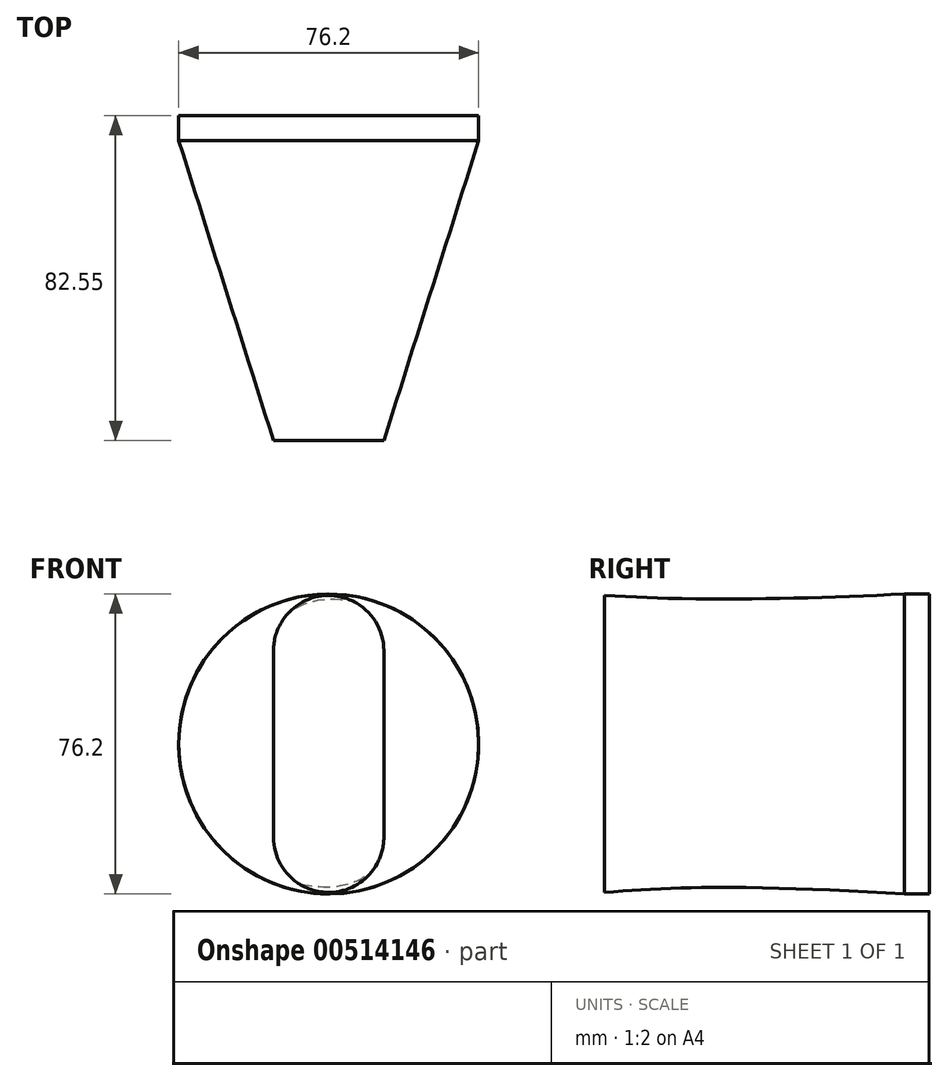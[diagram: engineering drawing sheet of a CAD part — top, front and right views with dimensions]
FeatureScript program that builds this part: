
annotation { "Feature Type Name" : "Feature", "Feature Type Description" : "" }
export const myFeature = defineFeature(function(context is Context, id is Id, definition is map)
    precondition{}
    {
        {
            var Q0;
            Q0=qCreatedBy(makeId("Front.planeOp"),FACE);
            var sketch = newSketch(context, id + "F0", { "sketchPlane" : qUnion([Q0])});
            skCircle(sketch, "E0", {"center": v(0, 0) * mm, "radius": 38.1 * mm});
            skSolve(sketch);
        }
        {
            var Q0;
            Q0=makeQuery(id+"F0.imprint","IMPRINT",FACE,{"disambiguationData":[TD([[makeQuery(id+"F0.imprint","IMPRINT",EDGE,{"derivedFrom":sQuery(id+"F0.wireOp",EDGE,"E0")}),1.0]])]});
            extrude(context, id + "F1", {"entities" : qUnion([Q0]), "oppositeDirection" : true, "depth" : 6.35 * mm, "offsetDistance" : 25.4 * mm});
        }
        {
            var Q0;
            Q0=qCreatedBy(makeId("Front.planeOp"),FACE);
            cPlane(context, id + "F2", {"entities" : qUnion([Q0]), "cplaneType" : CPlaneType.OFFSET, "offset" : 76.2 * mm, "width" : 152.4 * mm, "height" : 152.4 * mm});
        }
        {
            var Q0;
            Q0=qCreatedBy(id+"F2.planeOp",FACE);
            var sketch = newSketch(context, id + "F3", { "sketchPlane" : qUnion([Q0])});
            skLineSegment(sketch, "E1.bottom", {"start": v(-14.01, 23.7) * mm, "end": v(14.01, 23.7) * mm, "construction": true});
            skLineSegment(sketch, "E1.top", {"start": v(-14.01, -23.7) * mm, "end": v(14.01, -23.7) * mm, "construction": true});
            skLineSegment(sketch, "E1.left", {"start": v(-14.01, 23.7) * mm, "end": v(-14.01, -23.7) * mm});
            skLineSegment(sketch, "E1.right", {"start": v(14.01, 23.7) * mm, "end": v(14.01, -23.7) * mm});
            skPoint(sketch, "E1.middle", {"position": v(0, 0) * mm});
            skArc(sketch, "E2", {"start": v(0, 37.72) * mm, "mid": v(-9.9, 33.61) * mm, "end": v(-14.01, 23.7) * mm});
            skPoint(sketch, "E2.startSnap0", {"position": v(0, 23.7) * mm});
            skArc(sketch, "E3", {"start": v(0, 37.72) * mm, "mid": v(9.9, 33.61) * mm, "end": v(14.01, 23.7) * mm});
            skArc(sketch, "E4", {"start": v(1.97, -37.58) * mm, "mid": v(-9.19, -34.28) * mm, "end": v(-14.01, -23.7) * mm});
            skArc(sketch, "E5", {"start": v(1.97, -37.58) * mm, "mid": v(10.58, -32.89) * mm, "end": v(14.01, -23.7) * mm});
            skSolve(sketch);
        }
        {
            var Q0;
            Q0 = qSketchRegion(id + "F0", true);
            var Q1;
            Q1=makeQuery(id+"F3.imprint","IMPRINT",FACE,{"disambiguationData":[TD([[makeQuery(id+"F3.imprint","IMPRINT",EDGE,{"derivedFrom":sQuery(id+"F3.wireOp",EDGE,"E1.left")}),1.0]])]});
            loft(context, id + "F4", {"sheetProfilesArray" : [{ "sheetProfileEntities" : qUnion([Q0]) }, { "sheetProfileEntities" : qUnion([Q1]) }]});
        }
    });
